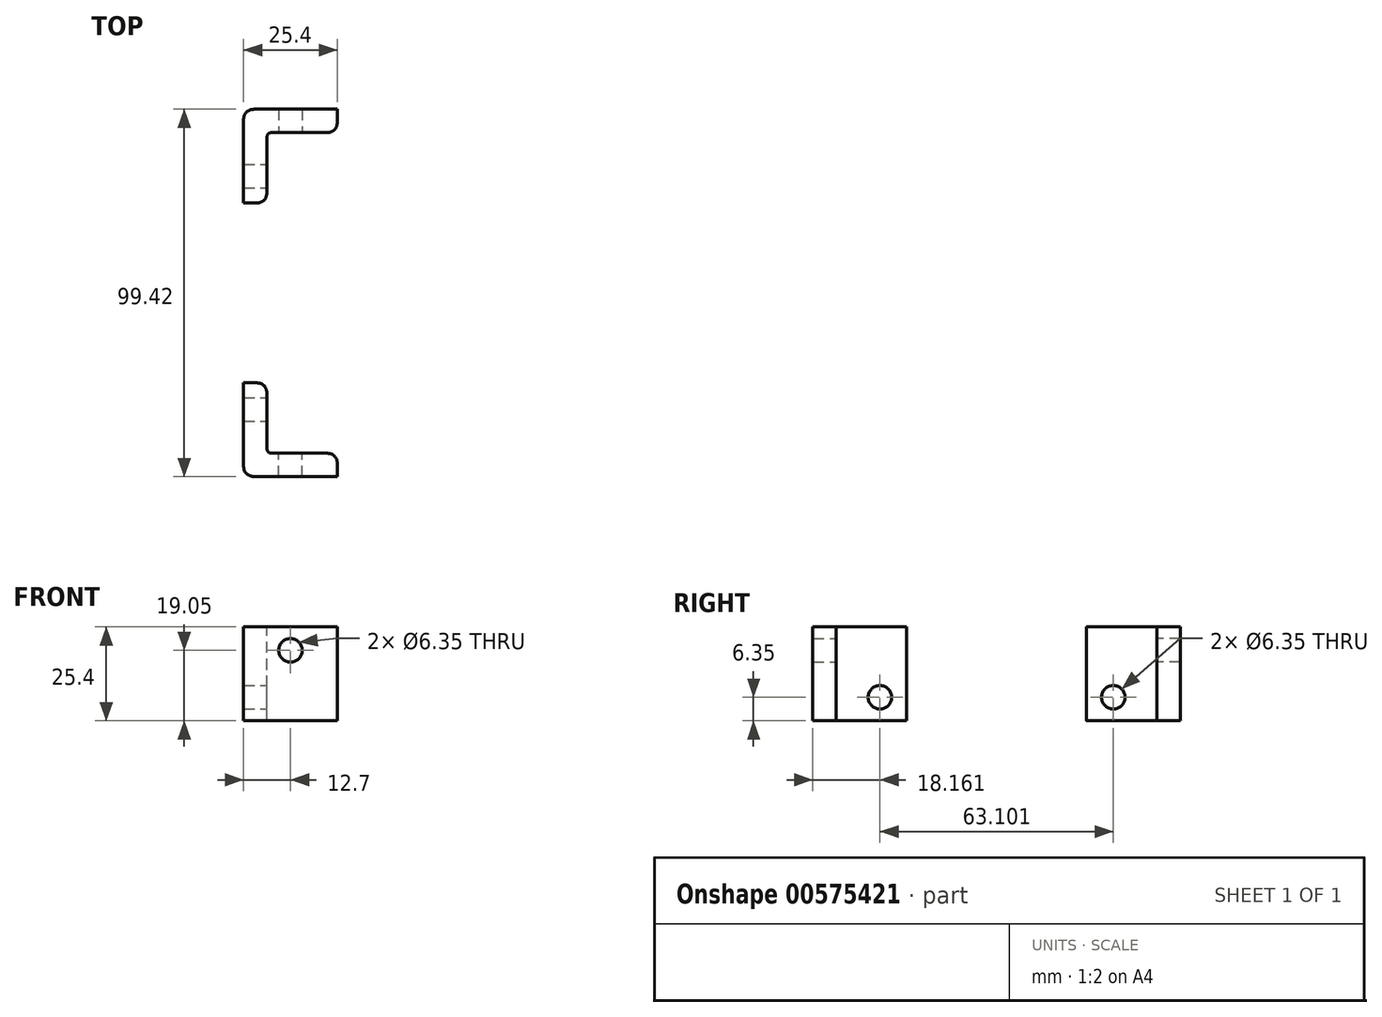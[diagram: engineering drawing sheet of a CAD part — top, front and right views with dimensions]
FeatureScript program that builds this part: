
annotation { "Feature Type Name" : "Feature", "Feature Type Description" : "" }
export const myFeature = defineFeature(function(context is Context, id is Id, definition is map)
    precondition{}
    {
        {
            var Q0;
            Q0=qCreatedBy(makeId("Top.planeOp"),FACE);
            var sketch = newSketch(context, id + "F0", { "sketchPlane" : qUnion([Q0])});
            skLineSegment(sketch, "E0", {"start": v(-39.15, 0) * mm, "end": v(-39.15, -25.4) * mm});
            skLineSegment(sketch, "E1", {"start": v(-39.15, -25.4) * mm, "end": v(-13.75, -25.4) * mm});
            skLineSegment(sketch, "E2", {"start": v(-13.75, -25.4) * mm, "end": v(-13.75, -19.05) * mm});
            skLineSegment(sketch, "E3", {"start": v(-13.75, -19.05) * mm, "end": v(-32.8, -19.05) * mm});
            skLineSegment(sketch, "E4", {"start": v(-32.8, -19.05) * mm, "end": v(-32.8, 0) * mm});
            skLineSegment(sketch, "E5", {"start": v(-32.8, 0) * mm, "end": v(-39.15, 0) * mm});
            skSolve(sketch);
        }
        {
            var Q0;
            Q0=makeQuery(id+"F0.imprint","IMPRINT",FACE,{"disambiguationData":[TD([[makeQuery(id+"F0.imprint","IMPRINT",EDGE,{"derivedFrom":sQuery(id+"F0.wireOp",EDGE,"E0")}),1.0]])]});
            extrude(context, id + "F1", {"entities" : qUnion([Q0]), "depth" : 25.4 * mm, "offsetDistance" : 25.4 * mm});
        }
        {
            var Q0;
            Q0=makeQuery(id+"F1.opExtrude","SWEPT_FACE",FACE,{"disambiguationData":[OSD([sQuery(id+"F0.wireOp",EDGE,"E4")])]});
            var sketch = newSketch(context, id + "F2", { "sketchPlane" : qUnion([Q0])});
            skCircle(sketch, "E6", {"center": v(-7.24, 6.35) * mm, "radius": 3.18 * mm});
            skSolve(sketch);
        }
        {
            var Q0;
            Q0=makeQuery(id+"F1.opExtrude","SWEPT_FACE",FACE,{"disambiguationData":[OSD([sQuery(id+"F0.wireOp",EDGE,"E3")])]});
            var sketch = newSketch(context, id + "F3", { "sketchPlane" : qUnion([Q0])});
            skCircle(sketch, "E7", {"center": v(26.45, 19.05) * mm, "radius": 3.17 * mm});
            skSolve(sketch);
        }
        {
            var Q0;
            Q0=makeQuery(id+"F3.imprint","IMPRINT",FACE,{"disambiguationData":[TD([[makeQuery(id+"F3.imprint","IMPRINT",EDGE,{"derivedFrom":sQuery(id+"F3.wireOp",EDGE,"E7")}),1.0]])]});
            extrude(context, id + "F4", {"entities" : qUnion([Q0]), "operationType" : NewBodyOperationType.REMOVE, "oppositeDirection" : true, "depth" : 6.35 * mm, "offsetDistance" : 25.4 * mm});
        }
        {
            var Q0;
            Q0=makeQuery(id+"F2.imprint","IMPRINT",FACE,{"disambiguationData":[TD([[makeQuery(id+"F2.imprint","IMPRINT",EDGE,{"derivedFrom":sQuery(id+"F2.wireOp",EDGE,"E6")}),1.0]])]});
            extrude(context, id + "F5", {"entities" : qUnion([Q0]), "operationType" : NewBodyOperationType.REMOVE, "oppositeDirection" : true, "depth" : 6.35 * mm, "offsetDistance" : 25.4 * mm});
        }
        {
            var Q0;
            Q0=qCreatedBy(makeId("Top.planeOp"),FACE);
            var sketch = newSketch(context, id + "F6", { "sketchPlane" : qUnion([Q0])});
            skLineSegment(sketch, "E8", {"start": v(-32.8, 48.62) * mm, "end": v(-32.8, 67.67) * mm});
            skLineSegment(sketch, "E9", {"start": v(-32.8, 67.67) * mm, "end": v(-13.75, 67.67) * mm});
            skLineSegment(sketch, "E10", {"start": v(-13.75, 67.67) * mm, "end": v(-13.75, 74.02) * mm});
            skLineSegment(sketch, "E11", {"start": v(-13.75, 74.02) * mm, "end": v(-39.15, 74.02) * mm});
            skLineSegment(sketch, "E12", {"start": v(-39.15, 74.02) * mm, "end": v(-39.15, 48.62) * mm});
            skLineSegment(sketch, "E13", {"start": v(-39.15, 48.62) * mm, "end": v(-32.8, 48.62) * mm});
            skSolve(sketch);
        }
        {
            var Q0;
            Q0=makeQuery(id+"F6.imprint","IMPRINT",FACE,{"disambiguationData":[TD([[makeQuery(id+"F6.imprint","IMPRINT",EDGE,{"derivedFrom":sQuery(id+"F6.wireOp",EDGE,"E8")}),1.0]])]});
            extrude(context, id + "F7", {"entities" : qUnion([Q0]), "depth" : 25.4 * mm, "offsetDistance" : 25.4 * mm});
        }
        {
            var Q0;
            Q0=makeQuery(id+"F7.opExtrude","SWEPT_FACE",FACE,{"disambiguationData":[OSD([sQuery(id+"F6.wireOp",EDGE,"E8")])]});
            var sketch = newSketch(context, id + "F8", { "sketchPlane" : qUnion([Q0])});
            skCircle(sketch, "E14", {"center": v(55.86, 6.35) * mm, "radius": 3.18 * mm});
            skSolve(sketch);
        }
        {
            var Q0;
            Q0=makeQuery(id+"F8.imprint","IMPRINT",FACE,{"disambiguationData":[TD([[makeQuery(id+"F8.imprint","IMPRINT",EDGE,{"derivedFrom":sQuery(id+"F8.wireOp",EDGE,"E14")}),1.0]])]});
            extrude(context, id + "F9", {"entities" : qUnion([Q0]), "operationType" : NewBodyOperationType.REMOVE, "oppositeDirection" : true, "depth" : 6.35 * mm, "offsetDistance" : 25.4 * mm});
        }
        {
            var Q0;
            Q0=makeQuery(id+"F7.opExtrude","SWEPT_FACE",FACE,{"disambiguationData":[OSD([sQuery(id+"F6.wireOp",EDGE,"E9")])]});
            var sketch = newSketch(context, id + "F10", { "sketchPlane" : qUnion([Q0])});
            skCircle(sketch, "E15", {"center": v(-26.45, 19.05) * mm, "radius": 3.18 * mm});
            skSolve(sketch);
        }
        {
            var Q0;
            Q0=makeQuery(id+"F10.imprint","IMPRINT",FACE,{"disambiguationData":[TD([[makeQuery(id+"F10.imprint","IMPRINT",EDGE,{"derivedFrom":sQuery(id+"F10.wireOp",EDGE,"E15")}),1.0]])]});
            extrude(context, id + "F11", {"entities" : qUnion([Q0]), "operationType" : NewBodyOperationType.REMOVE, "oppositeDirection" : true, "depth" : 6.35 * mm, "offsetDistance" : 25.4 * mm});
        }
        {
            var Q0;
            Q0=makeQuery(id+"F7.opExtrude","SWEPT_EDGE",EDGE,{"disambiguationData":[OSD([sQuery(id+"F6.wireOp",EDGE,"E9"),sQuery(id+"F6.wireOp",EDGE,"E10")])]});
            var Q1;
            Q1=makeQuery(id+"F7.opExtrude","SWEPT_EDGE",EDGE,{"disambiguationData":[OSD([sQuery(id+"F6.wireOp",EDGE,"E8"),sQuery(id+"F6.wireOp",EDGE,"E13")])]});
            var Q2;
            Q2=makeQuery(id+"F1.opExtrude","SWEPT_EDGE",EDGE,{"disambiguationData":[OSD([sQuery(id+"F0.wireOp",EDGE,"E4"),sQuery(id+"F0.wireOp",EDGE,"E5")])]});
            var Q3;
            Q3=makeQuery(id+"F1.opExtrude","SWEPT_EDGE",EDGE,{"disambiguationData":[OSD([sQuery(id+"F0.wireOp",EDGE,"E2"),sQuery(id+"F0.wireOp",EDGE,"E3")])]});
            fillet(context, id + "F12", {"entities" : qUnion([Q0, Q1, Q2, Q3]), "radius" : 3.17 * mm, "tangentPropagation" : true, "rho" : 0.5, "crossSection" : FilletCrossSection.CONIC, "allowEdgeOverflow" : false});
        }
        {
            var Q0;
            Q0=makeQuery(id+"F1.opExtrude","SWEPT_EDGE",EDGE,{"disambiguationData":[OSD([sQuery(id+"F0.wireOp",EDGE,"E0"),sQuery(id+"F0.wireOp",EDGE,"E1")])]});
            var Q1;
            Q1=makeQuery(id+"F7.opExtrude","SWEPT_EDGE",EDGE,{"disambiguationData":[OSD([sQuery(id+"F6.wireOp",EDGE,"E11"),sQuery(id+"F6.wireOp",EDGE,"E12")])]});
            fillet(context, id + "F13", {"entities" : qUnion([Q0, Q1]), "radius" : 3.17 * mm, "tangentPropagation" : true, "rho" : 0.5, "crossSection" : FilletCrossSection.CONIC, "allowEdgeOverflow" : false});
        }
        {
            var Q0;
            Q0=makeQuery(id+"F7.opExtrude","SWEPT_EDGE",EDGE,{"disambiguationData":[OSD([sQuery(id+"F6.wireOp",EDGE,"E8"),sQuery(id+"F6.wireOp",EDGE,"E9")])]});
            var Q1;
            Q1=makeQuery(id+"F1.opExtrude","SWEPT_EDGE",EDGE,{"disambiguationData":[OSD([sQuery(id+"F0.wireOp",EDGE,"E3"),sQuery(id+"F0.wireOp",EDGE,"E4")])]});
            fillet(context, id + "F14", {"entities" : qUnion([Q0, Q1]), "radius" : 1.27 * mm, "tangentPropagation" : true, "rho" : 0.5, "crossSection" : FilletCrossSection.CONIC, "allowEdgeOverflow" : false});
        }
    });
